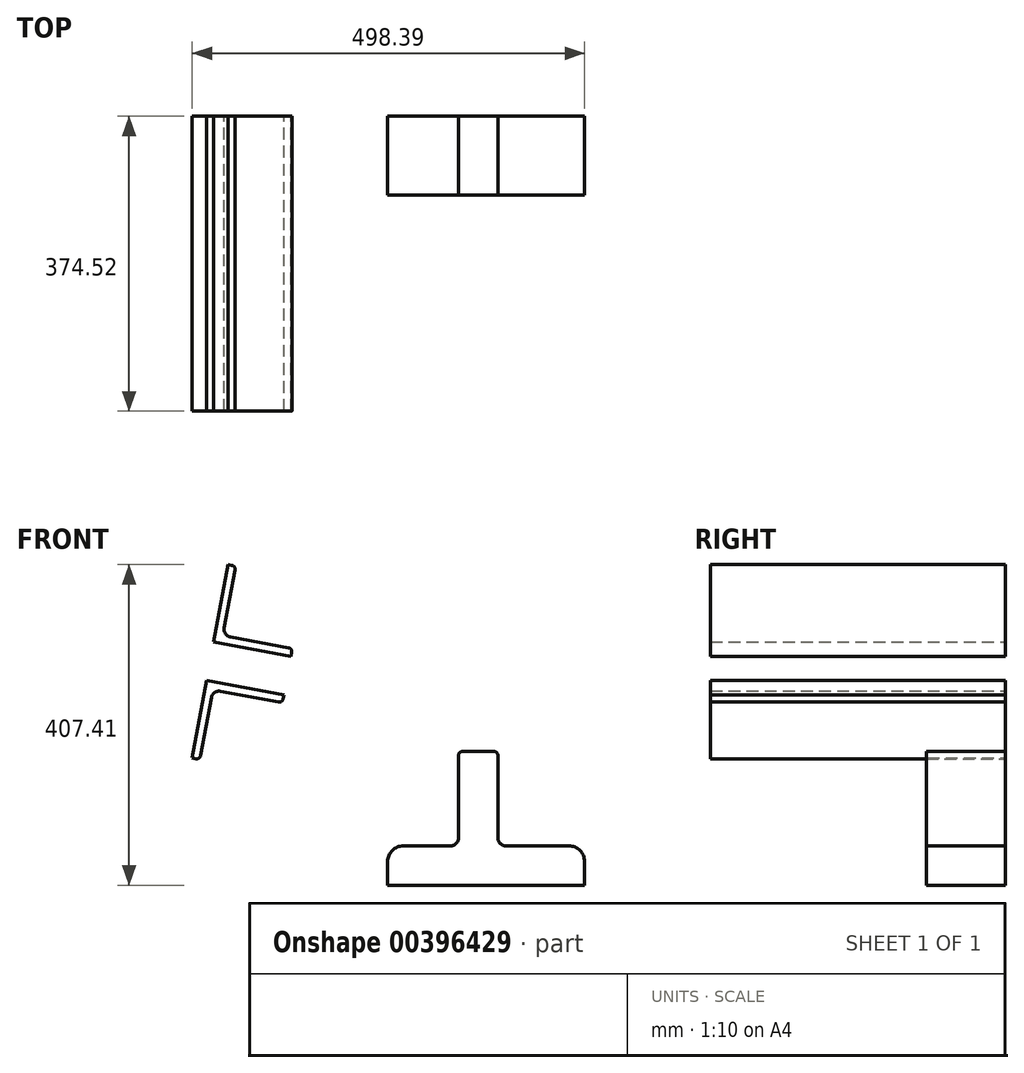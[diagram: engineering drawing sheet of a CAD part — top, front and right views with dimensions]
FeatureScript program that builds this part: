
annotation { "Feature Type Name" : "Feature", "Feature Type Description" : "" }
export const myFeature = defineFeature(function(context is Context, id is Id, definition is map)
    precondition{}
    {
        {
            var Q0;
            Q0=qCreatedBy(makeId("Front.planeOp"),FACE);
            var sketch = newSketch(context, id + "F0", { "sketchPlane" : qUnion([Q0])});
            skLineSegment(sketch, "E0", {"start": v(-27.89, -33.85) * mm, "end": v(-126.22, -15.67) * mm});
            skLineSegment(sketch, "E1", {"start": v(-126.22, -15.67) * mm, "end": v(-144.4, -114) * mm});
            skLineSegment(sketch, "E2", {"start": v(-144.4, -114) * mm, "end": v(-139.48, -114.91) * mm});
            skLineSegment(sketch, "E3", {"start": v(-133.66, -110.9) * mm, "end": v(-120.02, -37.16) * mm});
            skLineSegment(sketch, "E4", {"start": v(-108.37, -29.14) * mm, "end": v(-34.62, -42.77) * mm});
            skLineSegment(sketch, "E5", {"start": v(-28.8, -38.77) * mm, "end": v(-27.89, -33.85) * mm});
            skPoint(sketch, "E6.visualSharp", {"position": v(-29.7, -43.68) * mm});
            skArc(sketch, "E6.filletArc", {"start": v(-34.62, -42.77) * mm, "mid": v(-30.88, -41.98) * mm, "end": v(-28.8, -38.77) * mm});
            skPoint(sketch, "E7.visualSharp", {"position": v(-134.56, -115.82) * mm});
            skArc(sketch, "E7.filletArc", {"start": v(-139.48, -114.91) * mm, "mid": v(-135.74, -114.12) * mm, "end": v(-133.66, -110.9) * mm});
            skPoint(sketch, "E8.visualSharp", {"position": v(-118.2, -27.32) * mm});
            skArc(sketch, "E8.filletArc", {"start": v(-108.37, -29.14) * mm, "mid": v(-115.86, -30.74) * mm, "end": v(-120.02, -37.16) * mm});
            skSolve(sketch);
        }
        {
            var Q0;
            Q0=qCreatedBy(makeId("Front.planeOp"),FACE);
            var sketch = newSketch(context, id + "F1", { "sketchPlane" : qUnion([Q0])});
            skLineSegment(sketch, "E9", {"start": v(104, -275.58) * mm, "end": v(354, -275.58) * mm});
            skLineSegment(sketch, "E10", {"start": v(354, -275.58) * mm, "end": v(354, -245.58) * mm});
            skLineSegment(sketch, "E11", {"start": v(334, -225.58) * mm, "end": v(254, -225.58) * mm});
            skLineSegment(sketch, "E12", {"start": v(244, -215.58) * mm, "end": v(244, -110.58) * mm});
            skLineSegment(sketch, "E13", {"start": v(239, -105.58) * mm, "end": v(199, -105.58) * mm});
            skLineSegment(sketch, "E14", {"start": v(194, -110.58) * mm, "end": v(194, -215.58) * mm});
            skLineSegment(sketch, "E15", {"start": v(184, -225.58) * mm, "end": v(124, -225.58) * mm});
            skLineSegment(sketch, "E16", {"start": v(104, -245.58) * mm, "end": v(104, -275.58) * mm});
            skPoint(sketch, "E17.visualSharp", {"position": v(244, -225.58) * mm});
            skArc(sketch, "E17.filletArc", {"start": v(244, -215.58) * mm, "mid": v(246.92, -222.65) * mm, "end": v(254, -225.58) * mm});
            skPoint(sketch, "E18.visualSharp", {"position": v(194, -225.58) * mm});
            skArc(sketch, "E18.filletArc", {"start": v(184, -225.58) * mm, "mid": v(191.06, -222.65) * mm, "end": v(194, -215.58) * mm});
            skPoint(sketch, "E19.visualSharp", {"position": v(354, -225.58) * mm});
            skLineSegment(sketch, "E19.filletArc", {"start": v(354, -225.58) * mm, "end": v(354, -225.58) * mm});
            skPoint(sketch, "E20.visualSharp", {"position": v(104, -225.58) * mm});
            skLineSegment(sketch, "E20.filletArc", {"start": v(104, -225.58) * mm, "end": v(104, -225.58) * mm});
            skArc(sketch, "E21.filletArc", {"start": v(354, -245.58) * mm, "mid": v(348.13, -231.44) * mm, "end": v(334, -225.58) * mm});
            skArc(sketch, "E22.filletArc", {"start": v(124, -225.58) * mm, "mid": v(109.85, -231.44) * mm, "end": v(104, -245.58) * mm});
            skPoint(sketch, "E23.visualSharp", {"position": v(244, -105.58) * mm});
            skArc(sketch, "E23.filletArc", {"start": v(244, -110.58) * mm, "mid": v(242.53, -107.05) * mm, "end": v(239, -105.58) * mm});
            skPoint(sketch, "E24.visualSharp", {"position": v(194, -105.58) * mm});
            skArc(sketch, "E24.filletArc", {"start": v(199, -105.58) * mm, "mid": v(195.46, -107.05) * mm, "end": v(194, -110.58) * mm});
            skSolve(sketch);
        }
        {
            var Q0;
            Q0=makeQuery(id+"F0.imprint","IMPRINT",FACE,{"disambiguationData":[TD([[makeQuery(id+"F0.imprint","IMPRINT",EDGE,{"derivedFrom":sQuery(id+"F0.wireOp",EDGE,"E0")}),1.0]])]});
            extrude(context, id + "F2", {"entities" : qUnion([Q0]), "depth" : 374.52 * mm});
        }
        {
            var Q0;
            Q0=makeQuery(id+"F2.opExtrude","SWEPT_FACE",FACE,{"disambiguationData":[OSD([sQuery(id+"F0.wireOp",EDGE,"E0")])]});
            cPlane(context, id + "F3", {"entities" : qUnion([Q0]), "cplaneType" : CPlaneType.OFFSET, "offset" : 25 * mm, "width" : 150 * mm, "height" : 150 * mm});
        }
        {
            var Q0;
            Q0=makeQuery(id+"F2.opExtrude","SWEPT_BODY",BODY,{"disambiguationData":[OSD([sQuery(id+"F0.wireOp",EDGE,"E0"),sQuery(id+"F0.wireOp",EDGE,"E1"),sQuery(id+"F0.wireOp",EDGE,"E2"),sQuery(id+"F0.wireOp",EDGE,"E3"),sQuery(id+"F0.wireOp",EDGE,"E4"),sQuery(id+"F0.wireOp",EDGE,"E5"),sQuery(id+"F0.wireOp",EDGE,"E6.filletArc"),sQuery(id+"F0.wireOp",EDGE,"E7.filletArc"),sQuery(id+"F0.wireOp",EDGE,"E8.filletArc")])]});
            var Q1;
            Q1=qCreatedBy(id+"F3.planeOp",FACE);
            mirror(context, id + "F4", {"entities" : qUnion([Q0]), "mirrorPlane" : qUnion([Q1])});
        }
        {
            var Q0;
            Q0=makeQuery(id+"F1.imprint","IMPRINT",FACE,{"disambiguationData":[TD([[makeQuery(id+"F1.imprint","IMPRINT",EDGE,{"derivedFrom":sQuery(id+"F1.wireOp",EDGE,"E9")}),1.0]])]});
            extrude(context, id + "F5", {"entities" : qUnion([Q0]), "depth" : 100 * mm, "offsetDistance" : 25 * mm});
        }
    });
